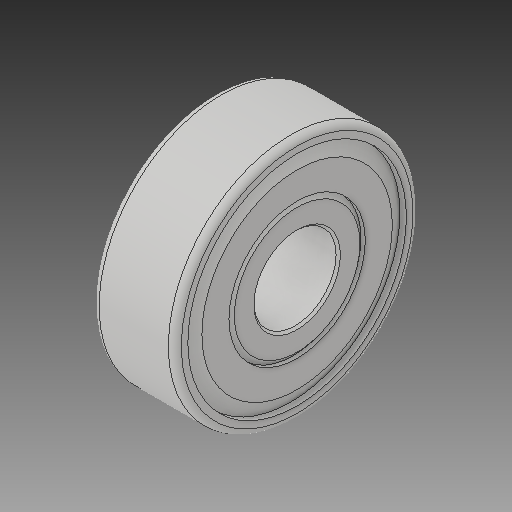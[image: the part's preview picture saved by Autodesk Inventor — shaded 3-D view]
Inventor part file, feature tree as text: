
AUTODESK INVENTOR PART (.ipt)
format: ipt  version: 2018 (Build 220112000, 112)  size: 177,664 bytes
history: native  units: in
note: dims shown in document units (in); Inventor stores cm internally (conversion verified against a paired STEP export)
features: chamfer x1
ambient origin geometry x8: Origin, YZ Plane, XZ Plane, XY Plane, X Axis, Y Axis, Z Axis, Center Point
bodies: Solid1 (feature_tree)
feature tree (1):
  chamfer  "Chamfer6"  [1 undecoded]
note: 1 required parameter value undecoded (feature->parameter linkage not recoverable at this tier; creation-order binding heuristic only, values carry confidence <= 0.55)
